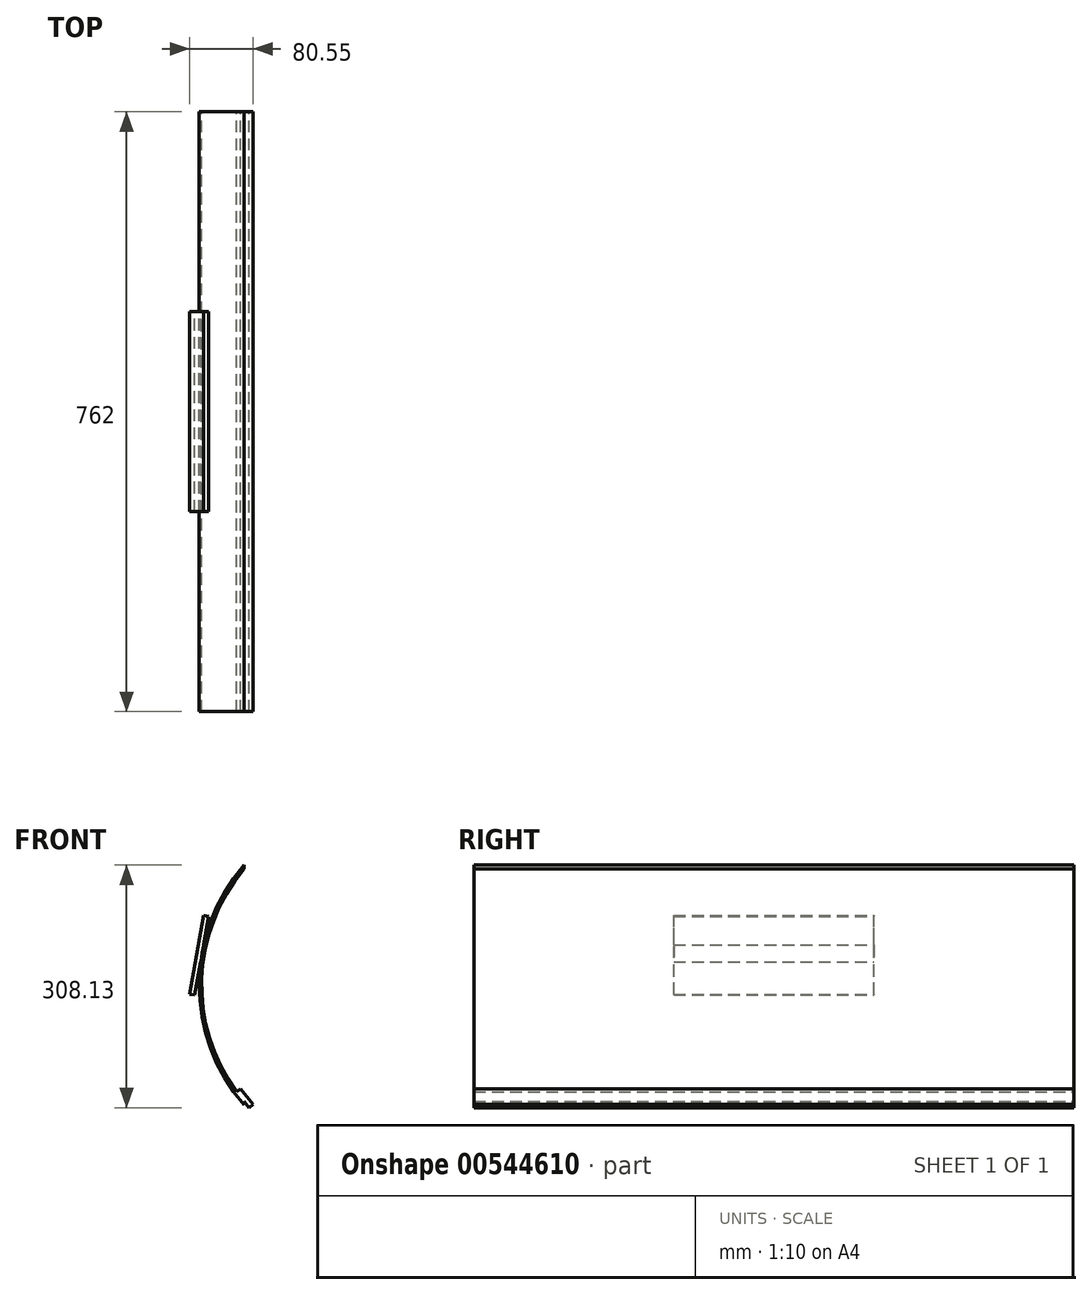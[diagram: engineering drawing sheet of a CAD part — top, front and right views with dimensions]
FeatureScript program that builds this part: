
annotation { "Feature Type Name" : "Feature", "Feature Type Description" : "" }
export const myFeature = defineFeature(function(context is Context, id is Id, definition is map)
    precondition{}
    {
        {
            var Q0;
            Q0=qCreatedBy(makeId("Front.planeOp"),FACE);
            var sketch = newSketch(context, id + "F0", { "sketchPlane" : qUnion([Q0])});
            skArc(sketch, "E0", {"start": v(-174.63, 147.53) * mm, "mid": v(-228.6, 0) * mm, "end": v(-174.63, -147.53) * mm});
            skArc(sketch, "E1.0", {"start": v(-174.63, 152.4) * mm, "mid": v(-231.78, 0) * mm, "end": v(-174.63, -152.4) * mm});
            skLineSegment(sketch, "E2", {"start": v(-174.63, 152.4) * mm, "end": v(-174.63, 147.53) * mm});
            skLineSegment(sketch, "E3.trimOffspring", {"start": v(-174.63, -147.53) * mm, "end": v(-174.63, -152.4) * mm});
            skSolve(sketch);
        }
        {
            var Q0;
            Q0 = qSketchRegion(id + "F0", true);
            extrude(context, id + "F1", {"entities" : qUnion([Q0]), "endBound" : BoundingType.SYMMETRIC, "depth" : 762 * mm, "offsetDistance" : 25.4 * mm});
        }
        {
            var Q0;
            Q0=qCreatedBy(makeId("Front.planeOp"),FACE);
            var sketch = newSketch(context, id + "F2", { "sketchPlane" : qUnion([Q0])});
            skArc(sketch, "E4.0", {"start": v(-174.63, 152.4) * mm, "mid": v(-231.78, 0) * mm, "end": v(-174.63, -152.4) * mm, "construction": true});
            skLineSegment(sketch, "E5", {"start": v(-237.59, -12.7) * mm, "end": v(-219.95, 87.36) * mm, "construction": true});
            skLineSegment(sketch, "E6", {"start": v(0, 0) * mm, "end": v(-285.96, 0) * mm, "construction": true});
            skLineSegment(sketch, "E7.0", {"start": v(-243.84, -11.6) * mm, "end": v(-226.2, 88.46) * mm});
            skLineSegment(sketch, "E8", {"start": v(-226.2, 88.46) * mm, "end": v(-219.7, 87.31) * mm});
            skLineSegment(sketch, "E9", {"start": v(-243.84, -11.6) * mm, "end": v(-237.34, -12.74) * mm});
            skLineSegment(sketch, "E10.0", {"start": v(-237.34, -12.74) * mm, "end": v(-219.7, 87.31) * mm});
            skSolve(sketch);
        }
        {
            var Q0;
            Q0=makeQuery(id+"F2.imprint","IMPRINT",FACE,{"disambiguationData":[TD([[makeQuery(id+"F2.imprint","IMPRINT",EDGE,{"derivedFrom":sQuery(id+"F2.wireOp",EDGE,"E5")}),1.0]])]});
            var Q1;
            Q1=makeQuery(id+"F2.imprint","IMPRINT",FACE,{"disambiguationData":[TD([[makeQuery(id+"F2.imprint","IMPRINT",EDGE,{"derivedFrom":sQuery(id+"F2.wireOp",EDGE,"E7.0")}),-1.0]])]});
            extrude(context, id + "F3", {"entities" : qUnion([Q0, Q1]), "operationType" : NewBodyOperationType.ADD, "endBound" : BoundingType.SYMMETRIC, "depth" : 254 * mm, "offsetDistance" : 25.4 * mm});
        }
        {
            var Q0;
            Q0=qCreatedBy(makeId("Front.planeOp"),FACE);
            var sketch = newSketch(context, id + "F4", { "sketchPlane" : qUnion([Q0])});
            skLineSegment(sketch, "E11", {"start": v(-168.27, -155.58) * mm, "end": v(-184.01, -135.64) * mm, "construction": true});
            skLineSegment(sketch, "E12.0", {"start": v(-174.63, -147.53) * mm, "end": v(-174.63, -152.4) * mm, "construction": true});
            skArc(sketch, "E13.0", {"start": v(-174.63, 147.53) * mm, "mid": v(-228.6, 0) * mm, "end": v(-174.63, -147.53) * mm, "construction": true});
            skLineSegment(sketch, "E14", {"start": v(-174.63, -152.4) * mm, "end": v(-168.91, -152.4) * mm, "construction": true});
            skLineSegment(sketch, "E15.0", {"start": v(-163.29, -151.64) * mm, "end": v(-179.03, -131.7) * mm});
            skLineSegment(sketch, "E16", {"start": v(-184.2, -135.8) * mm, "end": v(-179.03, -131.7) * mm});
            skLineSegment(sketch, "E17", {"start": v(-168.47, -155.73) * mm, "end": v(-163.29, -151.64) * mm});
            skLineSegment(sketch, "E18.0", {"start": v(-163.29, -151.64) * mm, "end": v(-179.03, -131.7) * mm, "construction": true});
            skLineSegment(sketch, "E19.0", {"start": v(-168.47, -155.73) * mm, "end": v(-184.2, -135.8) * mm});
            skSolve(sketch);
        }
        {
            var Q0;
            Q0 = qSketchRegion(id + "F4", true);
            extrude(context, id + "F5", {"entities" : qUnion([Q0]), "operationType" : NewBodyOperationType.ADD, "endBound" : BoundingType.SYMMETRIC, "depth" : 762 * mm, "offsetDistance" : 25.4 * mm});
        }
    });
